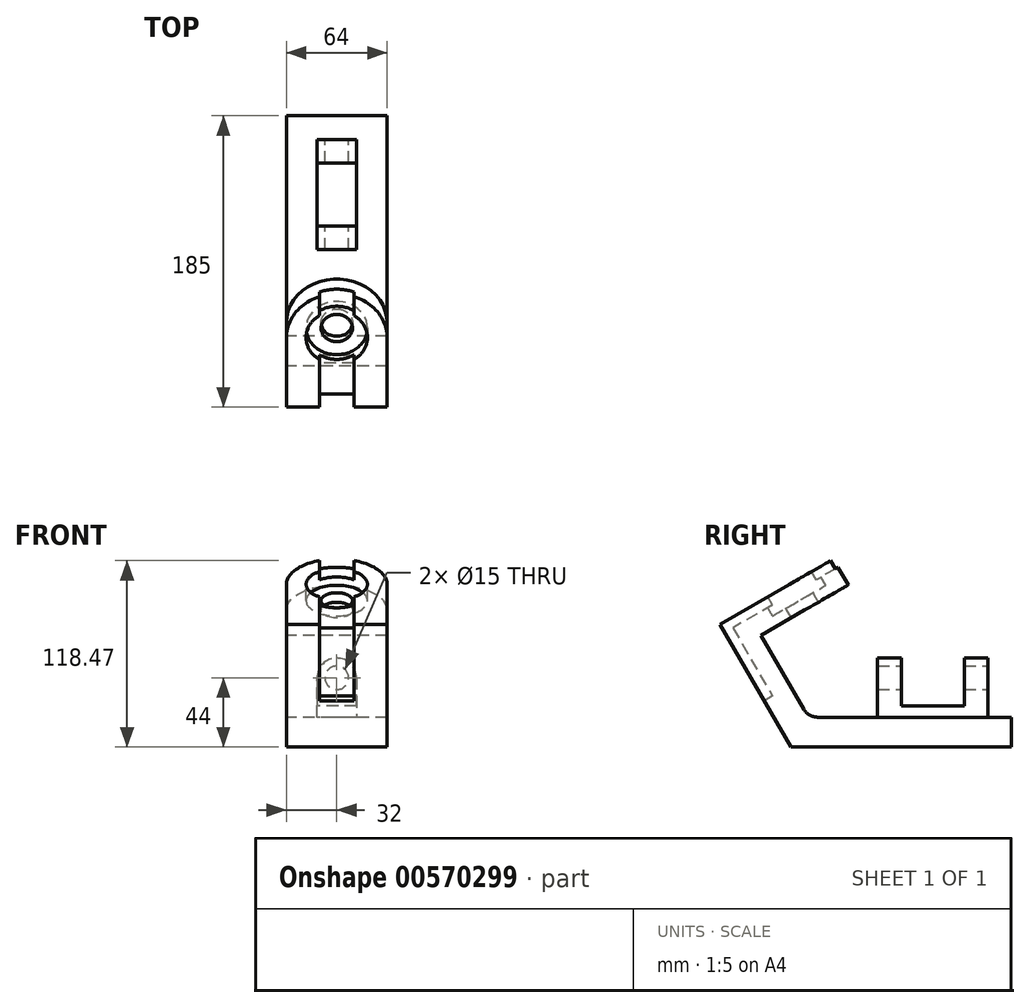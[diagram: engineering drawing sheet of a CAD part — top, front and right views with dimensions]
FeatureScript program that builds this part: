
annotation { "Feature Type Name" : "Feature", "Feature Type Description" : "" }
export const myFeature = defineFeature(function(context is Context, id is Id, definition is map)
    precondition{}
    {
        {
            var Q0;
            Q0=qCreatedBy(makeId("Right.planeOp"),FACE);
            var sketch = newSketch(context, id + "F0", { "sketchPlane" : qUnion([Q0])});
            skLineSegment(sketch, "E0", {"start": v(0, 0) * mm, "end": v(-45, 77.94) * mm});
            skLineSegment(sketch, "E1", {"start": v(-19.05, 70.99) * mm, "end": v(8.08, 24) * mm});
            skLineSegment(sketch, "E2", {"start": v(16.74, 19) * mm, "end": v(140, 19) * mm});
            skLineSegment(sketch, "E3", {"start": v(140, 19) * mm, "end": v(140, 0) * mm});
            skLineSegment(sketch, "E4", {"start": v(140, 0) * mm, "end": v(0, 0) * mm});
            skLineSegment(sketch, "E5", {"start": v(-17, 29.44) * mm, "end": v(-11.8, 32.44) * mm, "construction": true});
            skLineSegment(sketch, "E6", {"start": v(-11.8, 32.44) * mm, "end": v(-36.8, 75.75) * mm, "construction": true});
            skLineSegment(sketch, "E7", {"start": v(-36.8, 75.75) * mm, "end": v(39.38, 119.73) * mm, "construction": true});
            skLineSegment(sketch, "E8", {"start": v(-45, 77.94) * mm, "end": v(26.88, 119.44) * mm});
            skLineSegment(sketch, "E9", {"start": v(26.88, 119.44) * mm, "end": v(36.38, 102.99) * mm});
            skLineSegment(sketch, "E10", {"start": v(36.38, 102.99) * mm, "end": v(-19.05, 70.99) * mm});
            skLineSegment(sketch, "E11", {"start": v(-15.74, 129.26) * mm, "end": v(24.1, 60.26) * mm, "construction": true});
            skPoint(sketch, "E12.visualSharp", {"position": v(10.97, 19) * mm});
            skArc(sketch, "E12.filletArc", {"start": v(8.08, 24) * mm, "mid": v(11.74, 20.34) * mm, "end": v(16.74, 19) * mm});
            skSolve(sketch);
        }
        {
            var Q0;
            Q0 = qSketchRegion(id + "F0", true);
            extrude(context, id + "F1", {"entities" : qUnion([Q0]), "endBound" : BoundingType.SYMMETRIC, "depth" : 64 * mm, "offsetDistance" : 25 * mm});
        }
        {
            var Q0;
            Q0=makeQuery(id+"F1.opExtrude","SWEPT_FACE",FACE,{"disambiguationData":[OSD([sQuery(id+"F0.wireOp",EDGE,"E8")])]});
            var sketch = newSketch(context, id + "F2", { "sketchPlane" : qUnion([Q0])});
            skLineSegment(sketch, "E13", {"start": v(-32, 51) * mm, "end": v(-106.27, 51) * mm});
            skLineSegment(sketch, "E14", {"start": v(-106.27, 51) * mm, "end": v(-106.27, 125.27) * mm});
            skLineSegment(sketch, "E15", {"start": v(-106.27, 125.27) * mm, "end": v(106.27, 125.27) * mm});
            skLineSegment(sketch, "E16", {"start": v(106.27, 125.27) * mm, "end": v(106.27, 51) * mm});
            skLineSegment(sketch, "E17", {"start": v(106.27, 51) * mm, "end": v(32, 51) * mm});
            skArc(sketch, "E18", {"start": v(0, 83) * mm, "mid": v(-22.63, 73.63) * mm, "end": v(-32, 51) * mm});
            skArc(sketch, "E19", {"start": v(32, 51) * mm, "mid": v(22.63, 73.63) * mm, "end": v(0, 83) * mm});
            skSolve(sketch);
        }
        {
            var Q0;
            {var subQ0=sQuery(id+"F2.wireOp",EDGE,"E19");Q0=makeQuery(id+"F2.imprint","IMPRINT",FACE,{"disambiguationData":[TD([[makeQuery(id+"F2.imprint","IMPRINT",EDGE,{"derivedFrom":subQ0}),-1.0]])]});}
            var Q1;
            {var subQ0=sQuery(id+"F2.wireOp",EDGE,"E18");Q1=makeQuery(id+"F2.imprint","IMPRINT",FACE,{"disambiguationData":[TD([[makeQuery(id+"F2.imprint","IMPRINT",EDGE,{"derivedFrom":subQ0}),-1.0]])]});}
            var Q2;
            {var subQ6=sQuery(id+"F2.wireOp",EDGE,"E13");Q2=makeQuery(id+"F2.imprint","IMPRINT",FACE,{"disambiguationData":[TD([[makeQuery(id+"F2.imprint","IMPRINT",EDGE,{"derivedFrom":subQ6}),-1.0]])]});}
            var Q3;
            Q3=makeQuery(id+"F1.opExtrude","CAP_VERTEX",VERTEX,{"disambiguationData":[OSD([sQuery(id+"F0.wireOp",EDGE,"E9"),sQuery(id+"F0.wireOp",EDGE,"E10")])],"isStart":false});
            extrude(context, id + "F3", {"entities" : qUnion([Q0, Q1, Q2]), "operationType" : NewBodyOperationType.REMOVE, "endBound" : BoundingType.UP_TO_VERTEX, "oppositeDirection" : true, "depth" : 25 * mm, "endBoundEntityVertex" : qUnion([Q3]), "offsetDistance" : 25 * mm});
        }
        {
            var Q0;
            Q0=qCreatedBy(makeId("Right.planeOp"),FACE);
            var sketch = newSketch(context, id + "F4", { "sketchPlane" : qUnion([Q0])});
            skLineSegment(sketch, "E20", {"start": v(80.5, 143.48) * mm, "end": v(-36.8, 75.75) * mm});
            skLineSegment(sketch, "E21", {"start": v(-36.8, 75.75) * mm, "end": v(-11.8, 32.44) * mm});
            skLineSegment(sketch, "E22", {"start": v(-11.8, 32.44) * mm, "end": v(-58.72, 5.36) * mm});
            skLineSegment(sketch, "E23", {"start": v(-58.72, 5.36) * mm, "end": v(-109.4, 93.14) * mm});
            skLineSegment(sketch, "E24", {"start": v(-109.4, 93.14) * mm, "end": v(54.83, 187.96) * mm});
            skLineSegment(sketch, "E25", {"start": v(54.83, 187.96) * mm, "end": v(80.5, 143.48) * mm});
            skSolve(sketch);
        }
        {
            var Q0;
            Q0 = qSketchRegion(id + "F4", true);
            extrude(context, id + "F5", {"entities" : qUnion([Q0]), "operationType" : NewBodyOperationType.REMOVE, "endBound" : BoundingType.SYMMETRIC, "oppositeDirection" : true, "depth" : 22 * mm, "offsetDistance" : 25 * mm});
        }
        {
            var Q0;
            Q0=makeQuery(id+"F5.boolean.opBoolean","COPY",FACE,{"derivedFrom":makeQuery(id+"F5.opExtrude","SWEPT_FACE",FACE,{"disambiguationData":[OSD([sQuery(id+"F4.wireOp",EDGE,"E20")])]})});
            var sketch = newSketch(context, id + "F6", { "sketchPlane" : qUnion([Q0])});
            skCircle(sketch, "E26", {"center": v(0, 51) * mm, "radius": 10 * mm});
            skSolve(sketch);
        }
        {
            var Q0;
            Q0 = qSketchRegion(id + "F6", true);
            extrude(context, id + "F7", {"entities" : qUnion([Q0]), "operationType" : NewBodyOperationType.REMOVE, "endBound" : BoundingType.SYMMETRIC, "depth" : 50 * mm, "offsetDistance" : 25 * mm});
        }
        {
            var Q0;
            {var subQ1=sQuery(id+"F0.wireOp",EDGE,"E8");Q0=makeQuery(id+"F5.boolean.opBoolean","SPLIT",FACE,{"disambiguationData":[TD([makeQuery(id+"F5.opExtrude","CAP_FACE",FACE,{"disambiguationData":[OSD([sQuery(id+"F4.wireOp",EDGE,"E20"),sQuery(id+"F4.wireOp",EDGE,"E21"),sQuery(id+"F4.wireOp",EDGE,"E22"),sQuery(id+"F4.wireOp",EDGE,"E23"),sQuery(id+"F4.wireOp",EDGE,"E24"),sQuery(id+"F4.wireOp",EDGE,"E25")])],"isStart":false})])],"derivedFrom":makeQuery(id+"F1.opExtrude","SWEPT_FACE",FACE,{"disambiguationData":[OSD([subQ1])]})});}
            var sketch = newSketch(context, id + "F8", { "sketchPlane" : qUnion([Q0])});
            skCircle(sketch, "E27", {"center": v(0, 51) * mm, "radius": 19.5 * mm});
            skSolve(sketch);
        }
        {
            var Q0;
            Q0 = qSketchRegion(id + "F8", true);
            extrude(context, id + "F9", {"entities" : qUnion([Q0]), "operationType" : NewBodyOperationType.REMOVE, "oppositeDirection" : true, "depth" : 12 * mm, "offsetDistance" : 25 * mm});
        }
        {
            var Q0;
            Q0=makeQuery(id+"F1.opExtrude","SWEPT_FACE",FACE,{"disambiguationData":[OSD([sQuery(id+"F0.wireOp",EDGE,"E3")])]});
            cPlane(context, id + "F10", {"entities" : qUnion([Q0]), "cplaneType" : CPlaneType.OFFSET, "offset" : 15 * mm, "oppositeDirection" : true, "width" : 150 * mm, "height" : 150 * mm});
        }
        {
            var Q0;
            Q0=qCreatedBy(id+"F10.planeOp",FACE);
            var sketch = newSketch(context, id + "F11", { "sketchPlane" : qUnion([Q0])});
            skLineSegment(sketch, "E28", {"start": v(-12.5, 19) * mm, "end": v(12.5, 19) * mm});
            skLineSegment(sketch, "E29", {"start": v(12.5, 19) * mm, "end": v(12.5, 44) * mm});
            skLineSegment(sketch, "E30", {"start": v(12.5, 44) * mm, "end": v(-12.5, 44) * mm, "construction": true});
            skLineSegment(sketch, "E31", {"start": v(-12.5, 44) * mm, "end": v(-12.5, 19) * mm});
            skArc(sketch, "E32", {"start": v(12.5, 44) * mm, "mid": v(0, 56.5) * mm, "end": v(-12.5, 44) * mm});
            skCircle(sketch, "E33", {"center": v(0, 44) * mm, "radius": 7.5 * mm});
            skSolve(sketch);
        }
        {
            var Q0;
            Q0 = qSketchRegion(id + "F11", true);
            extrude(context, id + "F12", {"entities" : qUnion([Q0]), "operationType" : NewBodyOperationType.ADD, "oppositeDirection" : true, "depth" : 70 * mm, "offsetDistance" : 25 * mm});
        }
        {
            var Q0;
            Q0=qCreatedBy(makeId("Right.planeOp"),FACE);
            var sketch = newSketch(context, id + "F13", { "sketchPlane" : qUnion([Q0])});
            skLineSegment(sketch, "E34.bottom", {"start": v(70, 97.34) * mm, "end": v(110, 97.34) * mm});
            skLineSegment(sketch, "E34.top", {"start": v(70, 26) * mm, "end": v(110, 26) * mm});
            skLineSegment(sketch, "E34.left", {"start": v(70, 97.34) * mm, "end": v(70, 26) * mm});
            skLineSegment(sketch, "E34.right", {"start": v(110, 97.34) * mm, "end": v(110, 26) * mm});
            skLineSegment(sketch, "E35.0.0", {"start": v(125, 19) * mm, "end": v(125, 44) * mm, "construction": true});
            skLineSegment(sketch, "E35.0.1", {"start": v(125, 44) * mm, "end": v(55, 44) * mm, "construction": true});
            skLineSegment(sketch, "E35.0.2", {"start": v(55, 44) * mm, "end": v(55, 19) * mm, "construction": true});
            skLineSegment(sketch, "E35.0.3", {"start": v(55, 19) * mm, "end": v(125, 19) * mm, "construction": true});
            skLineSegment(sketch, "E36", {"start": v(90, 19) * mm, "end": v(90, 26) * mm});
            skSolve(sketch);
        }
        {
            var Q0;
            Q0 = qSketchRegion(id + "F13", true);
            extrude(context, id + "F14", {"entities" : qUnion([Q0]), "operationType" : NewBodyOperationType.REMOVE, "endBound" : BoundingType.SYMMETRIC, "depth" : 64 * mm, "offsetDistance" : 25 * mm});
        }
    });
